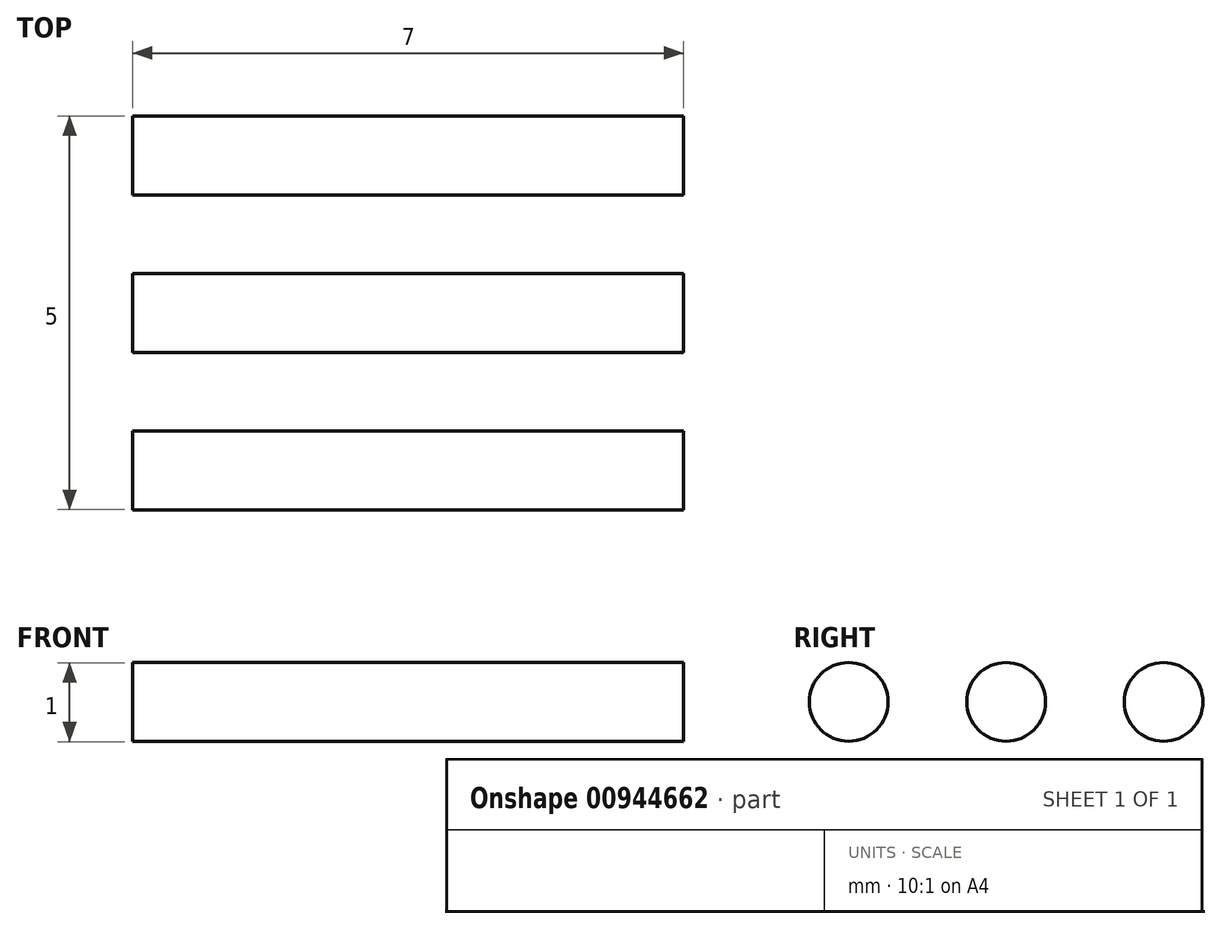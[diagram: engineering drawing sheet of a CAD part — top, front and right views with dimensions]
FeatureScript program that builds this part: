
annotation { "Feature Type Name" : "Feature", "Feature Type Description" : "" }
export const myFeature = defineFeature(function(context is Context, id is Id, definition is map)
    precondition{}
    {
        {
            var Q0;
            Q0=qCreatedBy(makeId("Right.planeOp"),FACE);
            var sketch = newSketch(context, id + "F0", { "sketchPlane" : qUnion([Q0])});
            skCircle(sketch, "E0", {"center": v(18, 44.08) * mm, "radius": 0.5 * mm});
            skLineSegment(sketch, "E1", {"start": v(18, 44.08) * mm, "end": v(10.88, 44.08) * mm, "construction": true});
            skCircle(sketch, "E2", {"center": v(16, 44.08) * mm, "radius": 0.5 * mm});
            skCircle(sketch, "E3", {"center": v(14, 44.08) * mm, "radius": 0.5 * mm});
            skSolve(sketch);
        }
        {
            var Q0;
            Q0=makeQuery(id+"F0.imprint","IMPRINT",FACE,{"disambiguationData":[TD([[makeQuery(id+"F0.imprint","IMPRINT",EDGE,{"derivedFrom":sQuery(id+"F0.wireOp",EDGE,"E0")}),1.0]])]});
            var Q1;
            Q1=makeQuery(id+"F0.imprint","IMPRINT",FACE,{"disambiguationData":[TD([[makeQuery(id+"F0.imprint","IMPRINT",EDGE,{"derivedFrom":sQuery(id+"F0.wireOp",EDGE,"E2")}),1.0]])]});
            var Q2;
            Q2=makeQuery(id+"F0.imprint","IMPRINT",FACE,{"disambiguationData":[TD([[makeQuery(id+"F0.imprint","IMPRINT",EDGE,{"derivedFrom":sQuery(id+"F0.wireOp",EDGE,"E3")}),1.0]])]});
            extrude(context, id + "F1", {"entities" : qUnion([Q0, Q1, Q2]), "depth" : 7 * mm, "offsetDistance" : 25.4 * mm});
        }
    });
